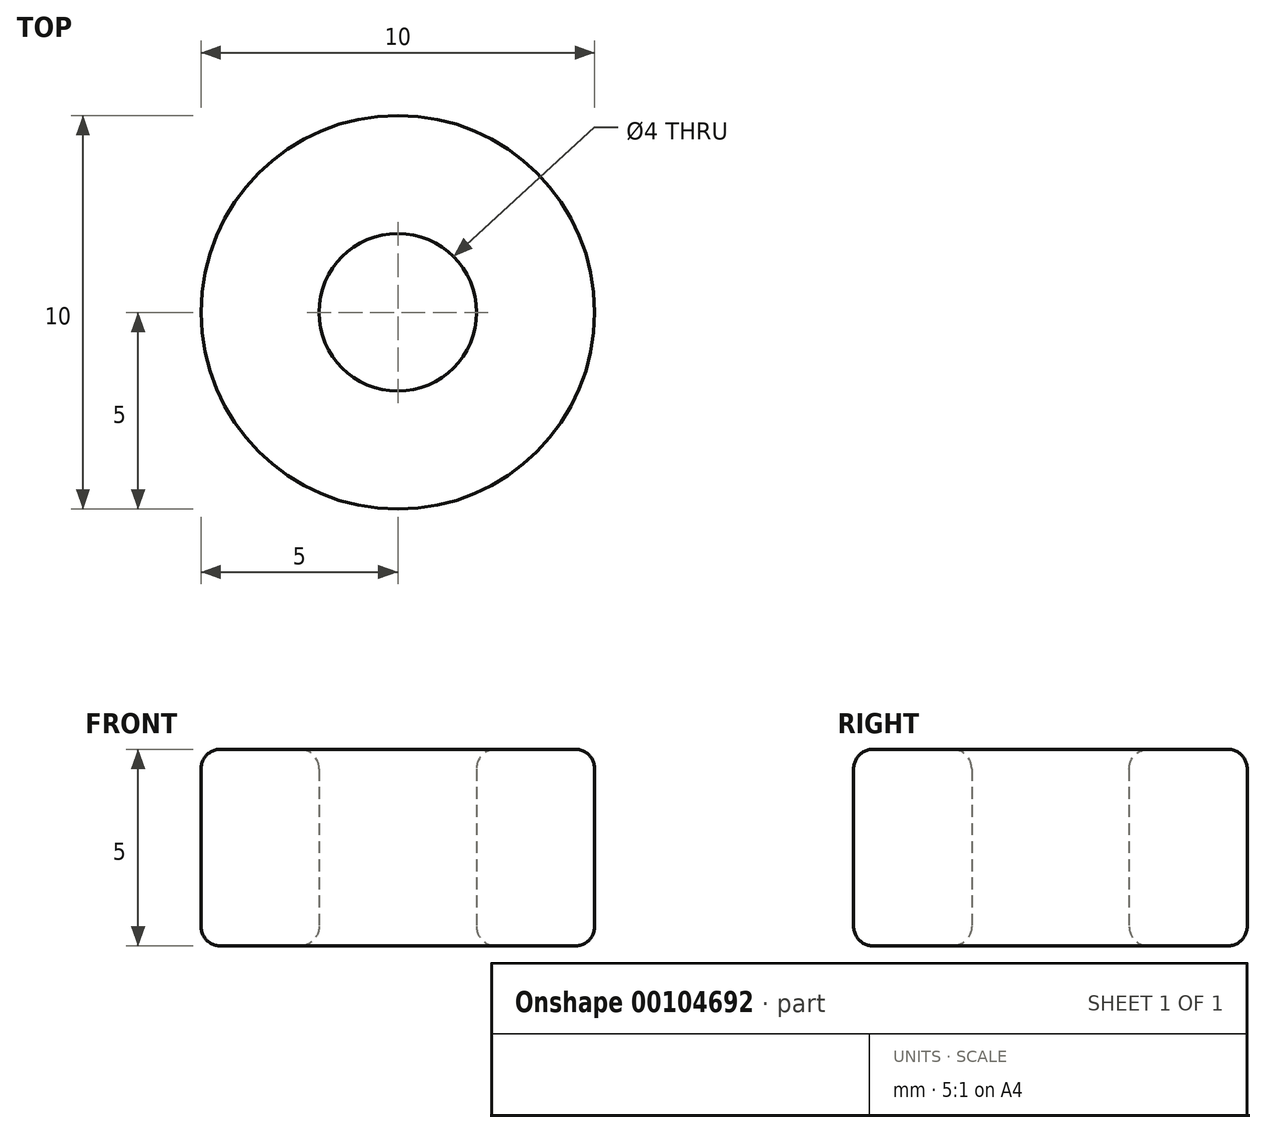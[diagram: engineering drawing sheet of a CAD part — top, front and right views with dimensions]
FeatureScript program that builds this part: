
annotation { "Feature Type Name" : "Feature", "Feature Type Description" : "" }
export const myFeature = defineFeature(function(context is Context, id is Id, definition is map)
    precondition{}
    {
        {
            var Q0;
            Q0=qCreatedBy(makeId("Top.planeOp"),FACE);
            var sketch = newSketch(context, id + "F0", { "sketchPlane" : qUnion([Q0])});
            skCircle(sketch, "E0", {"center": v(0, 0) * mm, "radius": 2 * mm});
            skCircle(sketch, "E1.0", {"center": v(0, 0) * mm, "radius": 5 * mm});
            skSolve(sketch);
        }
        {
            var Q0;
            Q0 = qSketchRegion(id + "F0", true);
            extrude(context, id + "F1", {"entities" : qUnion([Q0]), "depth" : 5 * mm});
        }
        {
            var Q0;
            Q0=makeQuery(id+"F1.opExtrude","CAP_FACE",FACE,{"disambiguationData":[OSD([sQuery(id+"F0.wireOp",EDGE,"E0"),sQuery(id+"F0.wireOp",EDGE,"E1.0")])],"isStart":false});
            var Q1;
            Q1=makeQuery(id+"F1.opExtrude","CAP_FACE",FACE,{"disambiguationData":[OSD([sQuery(id+"F0.wireOp",EDGE,"E0"),sQuery(id+"F0.wireOp",EDGE,"E1.0")])],"isStart":true});
            fillet(context, id + "F2", {"entities" : qUnion([Q0, Q1]), "radius" : .5 * mm, "tangentPropagation" : true, "allowEdgeOverflow" : false});
        }
    });
